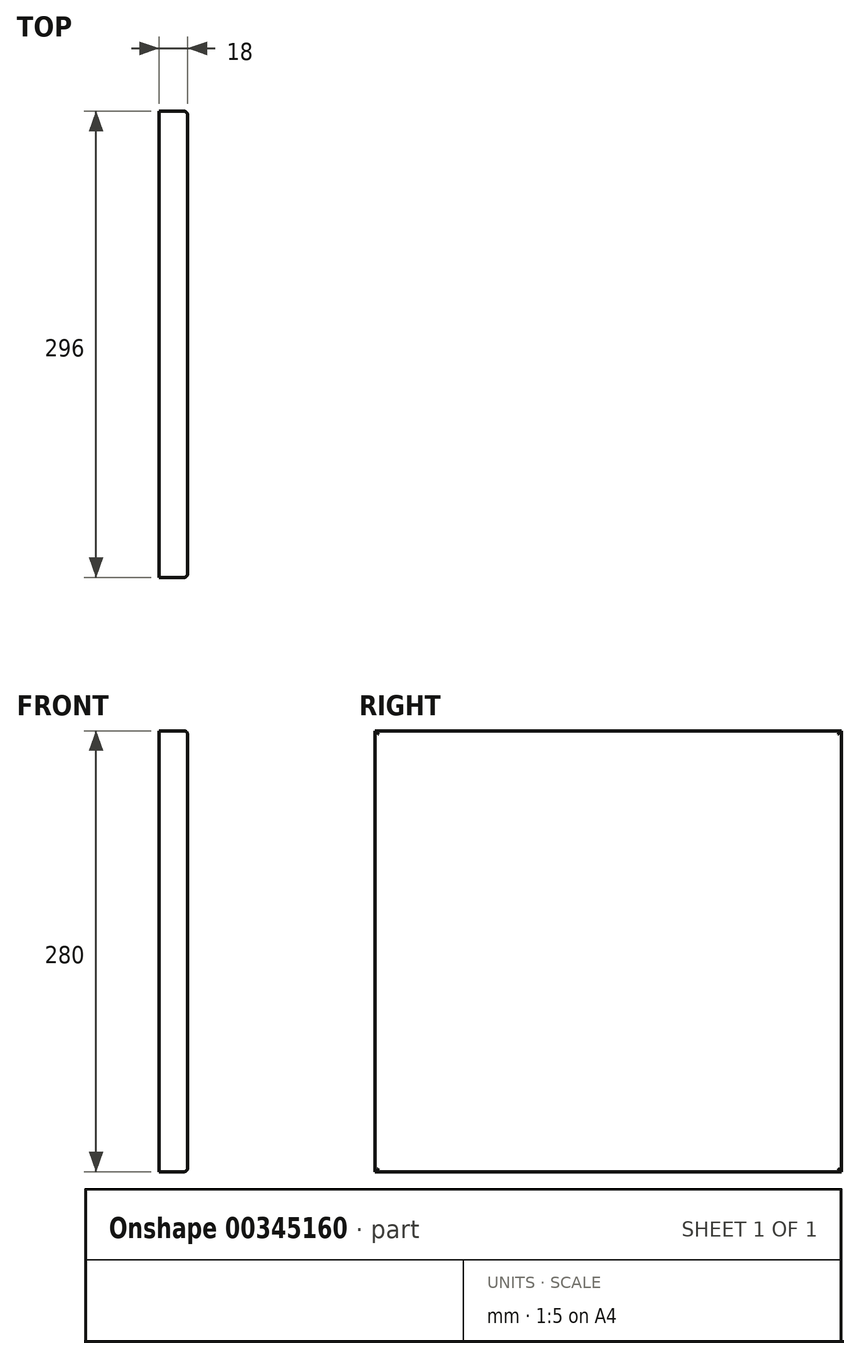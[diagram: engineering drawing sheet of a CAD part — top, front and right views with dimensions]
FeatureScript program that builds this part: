
annotation { "Feature Type Name" : "Feature", "Feature Type Description" : "" }
export const myFeature = defineFeature(function(context is Context, id is Id, definition is map)
    precondition{}
    {
        {
            var Q0;
            Q0=qCreatedBy(makeId("Right.planeOp"),FACE);
            var sketch = newSketch(context, id + "F0", { "sketchPlane" : qUnion([Q0])});
            skLineSegment(sketch, "E0.bottom", {"start": v(0, 0) * mm, "end": v(-42.6, 0) * mm});
            skLineSegment(sketch, "E0.top", {"start": v(0, 36.73) * mm, "end": v(-42.6, 36.73) * mm});
            skLineSegment(sketch, "E0.left", {"start": v(0, 0) * mm, "end": v(0, 36.73) * mm});
            skLineSegment(sketch, "E0.right", {"start": v(-42.6, 0) * mm, "end": v(-42.6, 36.73) * mm});
            skSolve(sketch);
        }
        {
            var Q0;
            Q0=makeQuery(id+"F0.imprint","IMPRINT",FACE,{"disambiguationData":[TD([[makeQuery(id+"F0.imprint","IMPRINT",EDGE,{"derivedFrom":sQuery(id+"F0.wireOp",EDGE,"E0.bottom")}),-1.0]])]});
            extrude(context, id + "F1", {"entities" : qUnion([Q0]), "oppositeDirection" : true, "depth" : 18 * mm});
        }
        {
            var Q0;
            Q0=makeQuery(id+"F1.opExtrude","SWEPT_FACE",FACE,{"disambiguationData":[OSD([sQuery(id+"F0.wireOp",EDGE,"E0.bottom")])]});
            extrude(context, id + "F2", {"entities" : qUnion([Q0]), "operationType" : NewBodyOperationType.ADD, "oppositeDirection" : true, "depth" : 282 * mm});
        }
        {
            var Q0;
            {var subQ0=sQuery(id+"F0.wireOp",EDGE,"E0.left");Q0=makeQuery(id+"F2.boolean.opBoolean","MERGE",FACE,{"derivedFrom":[makeQuery(id+"F1.opExtrude","SWEPT_FACE",FACE,{"disambiguationData":[OSD([subQ0])]}),makeQuery(id+"F2.opExtrude","SWEPT_FACE",FACE,{"disambiguationData":[OSD([sQuery(id+"F0.wireOp",EDGE,"E0.bottom"),subQ0])]})]});}
            extrude(context, id + "F3", {"entities" : qUnion([Q0]), "operationType" : NewBodyOperationType.ADD, "oppositeDirection" : true, "depth" : 296 * mm});
        }
        {
            var Q0;
            {var subQ0=sQuery(id+"F0.wireOp",EDGE,"E0.left");var subQ1=sQuery(id+"F0.wireOp",EDGE,"E0.bottom");Q0=makeQuery(id+"F3.boolean.opBoolean","MERGE",FACE,{"derivedFrom":[makeQuery(id+"F1.opExtrude","SWEPT_FACE",FACE,{"disambiguationData":[OSD([subQ1])]}),makeQuery(id+"F3.opExtrude","SWEPT_FACE",FACE,{"disambiguationData":[OSD([subQ1,subQ0]),TDD([makeQuery(id+"F1.opExtrude","SWEPT_EDGE",EDGE,{"disambiguationData":[OSD([subQ1,subQ0])]})])]})]});}
            extrude(context, id + "F4", {"entities" : qUnion([Q0]), "operationType" : NewBodyOperationType.INTERSECT, "oppositeDirection" : true, "depth" : 280 * mm});
        }
        {
            var Q0;
            {var subQ0=sQuery(id+"F0.wireOp",EDGE,"E0.left");var subQ1=sQuery(id+"F0.wireOp",EDGE,"E0.bottom");Q0=makeQuery(id+"F3.boolean.opBoolean","MERGE",FACE,{"derivedFrom":[makeQuery(id+"F2.boolean.opBoolean","MERGE",FACE,{"derivedFrom":[makeQuery(id+"F1.opExtrude","CAP_FACE",FACE,{"disambiguationData":[OSD([subQ1,sQuery(id+"F0.wireOp",EDGE,"E0.top"),subQ0,sQuery(id+"F0.wireOp",EDGE,"E0.right")])],"isStart":true}),makeQuery(id+"F2.opExtrude","SWEPT_FACE",FACE,{"disambiguationData":[OSD([subQ1]),TDD([makeQuery(id+"F1.opExtrude","CAP_EDGE",EDGE,{"disambiguationData":[OSD([subQ1])],"isStart":true})])]})]}),makeQuery(id+"F3.opExtrude","SWEPT_FACE",FACE,{"disambiguationData":[OSD([subQ1,subQ0]),TDD([makeQuery(id+"F2.boolean.opBoolean","MERGE",EDGE,{"derivedFrom":[makeQuery(id+"F1.opExtrude","CAP_EDGE",EDGE,{"disambiguationData":[OSD([subQ0])],"isStart":true}),makeQuery(id+"F2.opExtrude","SWEPT_EDGE",EDGE,{"disambiguationData":[OSD([subQ1,subQ0]),TDD([makeQuery(id+"F1.opExtrude","CAP_VERTEX",VERTEX,{"disambiguationData":[OSD([subQ1,subQ0])],"isStart":true})])]})]})])]})]});}
            fillet(context, id + "F5", {"entities" : qUnion([Q0]), "radius" : 2 * mm, "tangentPropagation" : true, "allowEdgeOverflow" : false});
        }
    });
